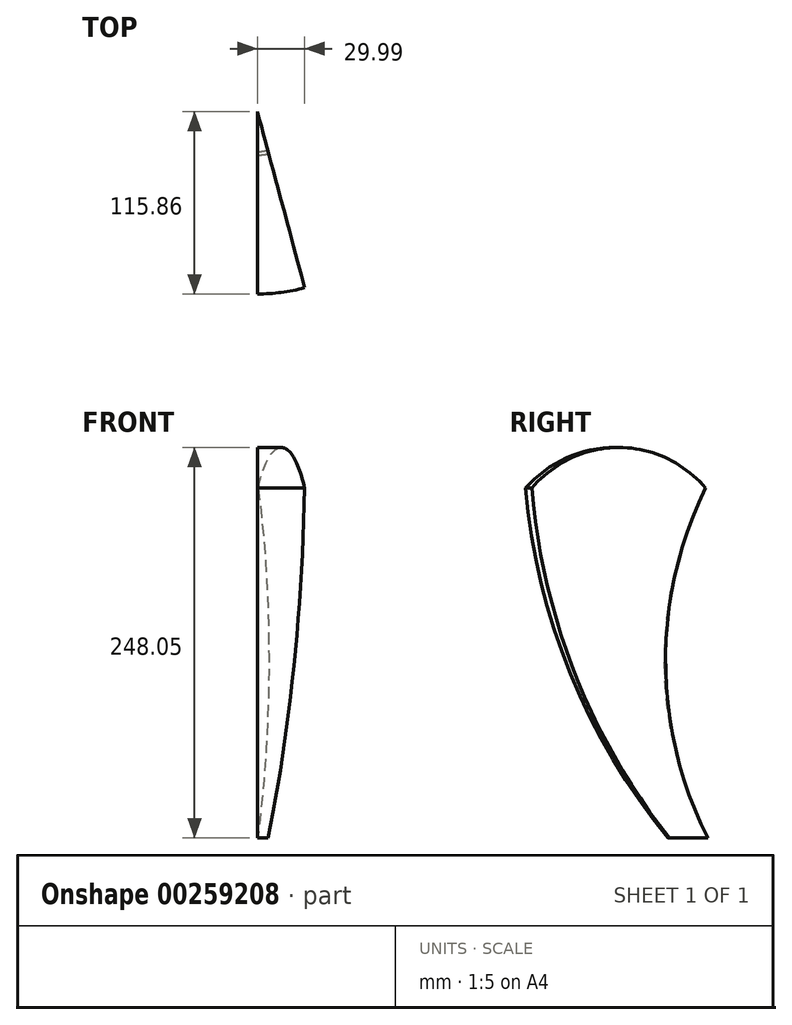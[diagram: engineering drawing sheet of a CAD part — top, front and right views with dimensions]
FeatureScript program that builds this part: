
annotation { "Feature Type Name" : "Feature", "Feature Type Description" : "" }
export const myFeature = defineFeature(function(context is Context, id is Id, definition is map)
    precondition{}
    {
        {
            var Q0;
            Q0=qCreatedBy(makeId("Right.planeOp"),FACE);
            var sketch = newSketch(context, id + "F0", { "sketchPlane" : qUnion([Q0])});
            skArc(sketch, "E0", {"start": v(-115.86, 222.25) * mm, "mid": v(-87.4, 104.3) * mm, "end": v(-25.4, 0) * mm});
            skArc(sketch, "E1", {"start": v(-1.56, 222.25) * mm, "mid": v(-27.9, 110.93) * mm, "end": v(0, 0) * mm});
            skArc(sketch, "E2", {"start": v(-1.56, 222.25) * mm, "mid": v(-58.7, 248.05) * mm, "end": v(-115.86, 222.25) * mm});
            skLineSegment(sketch, "E3", {"start": v(0, 0) * mm, "end": v(-25.4, 0) * mm});
            skSolve(sketch);
        }
        {
            var Q0;
            Q0=qCreatedBy(makeId("Right.planeOp"),FACE);
            var sketch = newSketch(context, id + "F1", { "sketchPlane" : qUnion([Q0])});
            skLineSegment(sketch, "E4", {"start": v(0, 0) * mm, "end": v(0, 127) * mm, "construction": true});
            skSolve(sketch);
        }
        {
            var Q0;
            Q0 = qSketchRegion(id + "F0", true);
            var Q1;
            Q1=sQuery(id+"F1.wireOp",EDGE,"E4");
            var Q2;
            Q2 = qConstructionFilter(qBodyType(qCreatedBy(id + "F0" ,EDGE), BodyType.WIRE), ConstructionObject.NO);
            var Q3;
            Q3=sQuery(id+"F1.wireOp",EDGE,"E4");
            revolve(context, id + "F2", {"entities" : qUnion([Q0]), "surfaceEntities" : qUnion([Q1, Q2]), "axis" : qUnion([Q3]), "revolveType" : RevolveType.ONE_DIRECTION, "angle" : 15 * degree});
        }
    });
